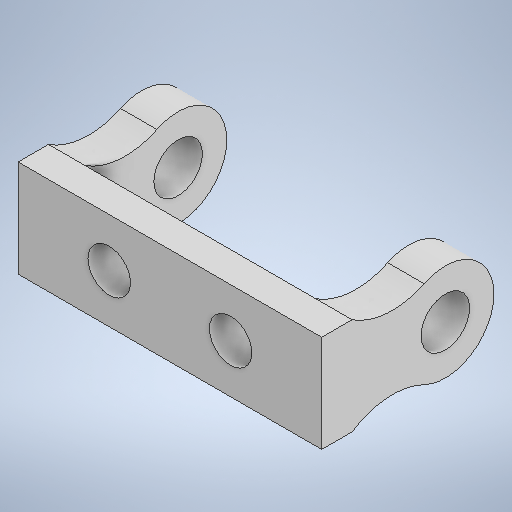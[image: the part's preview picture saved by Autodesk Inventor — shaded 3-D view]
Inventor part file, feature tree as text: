
AUTODESK INVENTOR PART (.ipt)
format: ipt  version: 2025 (Build 290162010, 162A)  size: 272,896 bytes
history: native  units: mm
features: sketch x2, extrude x2, plane x1, mirror x1, hole x1
ambient origin geometry x8: Origin, YZ Plane, XZ Plane, XY Plane, X Axis, Y Axis, Z Axis, Center Point
bodies: Volumenkörper1 (feature_tree)
feature tree (7):
  sketch  "Skizze1"  dims[d7=13.0mm d9=2.5mm]
  extrude  "Extrusion1"  Depth=2.5mm
  extrude  "Extrusion2"  Depth=10.0mm
  plane  "Arbeitsebene1"
  mirror  "Spiegeln1"
  hole  "Bohrung1"  [1 undecoded]
  sketch  "Skizze2"  dims[d10=12.0mm d11=12.0mm d15=8.0mm d16=18.0mm d17=25.0mm d18=0.0mm d19=3.0mm d20=0.0mm d21=4.0mm d22=12.5mm d23=3.5mm d24=6.0mm d25=4.0mm d26=2.0mm d27=90.0deg d28=8.0mm d29=0.0mm d30=10.0mm d31=4.5mm d32=0.5mm d33=0.872665mm d34=0.5mm d35=0.872665mm]
note: 1 required parameter value undecoded (feature->parameter linkage not recoverable at this tier; creation-order binding heuristic only, values carry confidence <= 0.55)
